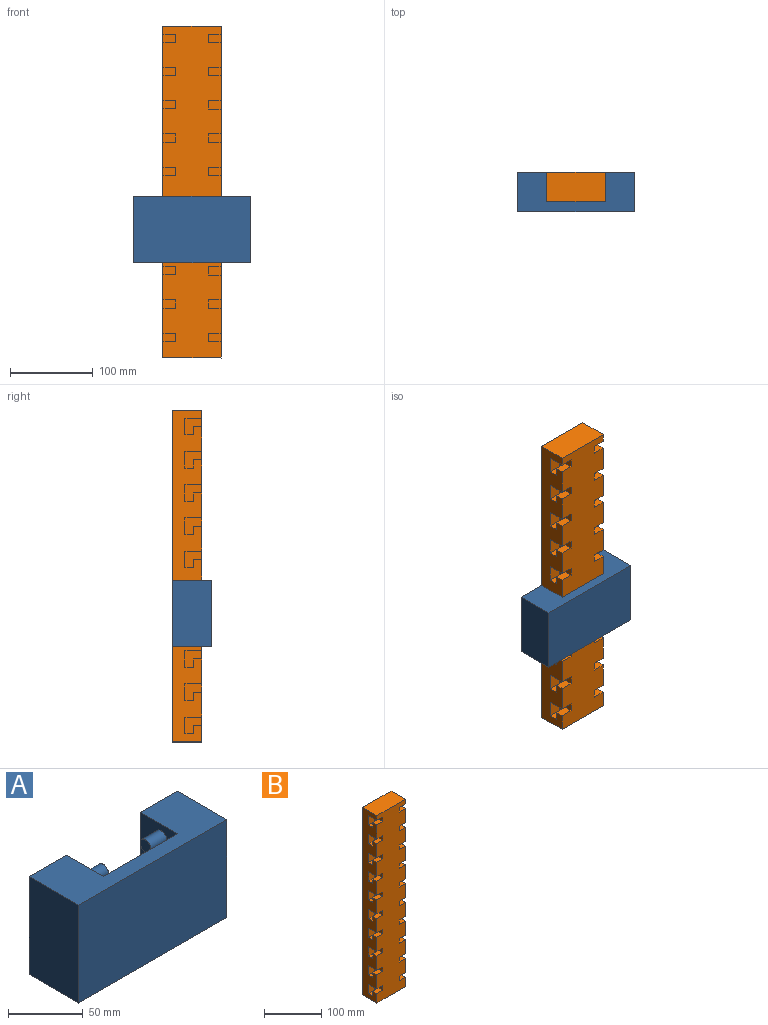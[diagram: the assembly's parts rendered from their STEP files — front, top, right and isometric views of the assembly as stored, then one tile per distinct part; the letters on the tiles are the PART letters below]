
ASSEMBLY  parts=2 mates=1
PART A: 18 faces, bbox 140x47x80 mm
  f0: plane 80x35mm, normal (1,0,0), area 2642.9mm2, adj f1,f3,f9,f10,f12,f16
  f1: plane 140x47mm, normal (0,0,-1), area 4130mm2, adj f0,f2,f3,f4,f5,f6,f9,f11
  f2: plane 80x47mm, normal (-1,0,0), area 3760mm2, adj f1,f3,f10,f11
  f3: plane 80x35mm, normal (0,1,0), area 2800mm2, adj f0,f1,f2,f10
  f4: plane 80x35mm, normal (-1,0,0), area 2642.9mm2, adj f1,f6,f7,f9,f10,f14
  f5: plane 80x47mm, normal (1,0,0), area 3760mm2, adj f1,f6,f10,f11
  f6: plane 80x35mm, normal (0,1,0), area 2800mm2, adj f1,f4,f5,f10
  f7: cylinder r=5mm len=15mm, axis (1,0,0), area 471.2mm2, adj f4,f8
  f8: plane 10x10mm, normal (-1,0,0), area 78.5mm2, adj f7
  f9: plane 80x70mm, normal (0,1,0), area 5600mm2, adj f0,f1,f4,f10
  f10: plane 140x47mm, normal (0,0,1), area 4130mm2, adj f0,f2,f3,f4,f5,f6,f9,f11
  f11: plane 140x80mm, normal (0,-1,0), area 11200mm2, adj f1,f2,f5,f10
  f12: cylinder r=5mm len=15mm, axis (1,0,0), area 471.2mm2, adj f0,f13
  f13: plane 10x10mm, normal (1,0,0), area 78.5mm2, adj f12
  f14: cylinder r=5mm len=15mm, axis (1,0,0), area 471.2mm2, adj f4,f15
  f15: plane 10x10mm, normal (-1,0,0), area 78.5mm2, adj f14
  f16: cylinder r=5mm len=15mm, axis (1,0,0), area 471.2mm2, adj f0,f17
  f17: plane 10x10mm, normal (1,0,0), area 78.5mm2, adj f16
PART B: 126 faces, bbox 70x35x400 mm
  f0: plane 20x15mm, normal (0,-1,0), area 300mm2, adj f1,f2,f7,f16
  f1: plane 20x15mm, normal (0,0,-1), area 300mm2, adj f0,f7,f8,f16
  f2: plane 15x10mm, normal (0,0,1), area 150mm2, adj f0,f7,f13,f16
  f3: plane 15x10mm, normal (0,0,1), area 150mm2, adj f4,f5,f8,f15
  f4: plane 15x10mm, normal (0,1,0), area 150mm2, adj f3,f5,f14,f15
  f5: plane 400x35mm, normal (-1,0,0), area 11000mm2, adj f3,f4,f6,f8,f9,f10,f11,f14
  f6: plane 70x35mm, normal (0,0,-1), area 2450mm2, adj f5,f7,f8,f9
  f7: plane 400x35mm, normal (1,0,0), area 11000mm2, adj f0,f1,f2,f6,f8,f9,f12,f13
  f8: plane 400x70mm, normal (0,-1,0), area 25000mm2, adj f1,f3,f5,f6,f7,f11,f12,f15
  f9: plane 400x70mm, normal (0,1,0), area 28000mm2, adj f5,f6,f7,f118
  f10: plane 20x15mm, normal (0,-1,0), area 300mm2, adj f5,f11,f14,f15
  f11: plane 20x15mm, normal (0,0,-1), area 300mm2, adj f5,f8,f10,f15
  f12: plane 15x10mm, normal (0,0,1), area 150mm2, adj f7,f8,f13,f16
  f13: plane 15x10mm, normal (0,1,0), area 150mm2, adj f2,f7,f12,f16
  f14: plane 15x10mm, normal (0,0,1), area 150mm2, adj f4,f5,f10,f15
  f15: plane 20x20mm, normal (-1,0,0), area 300mm2, adj f3,f4,f8,f10,f11,f14
  f16: plane 20x20mm, normal (1,0,0), area 300mm2, adj f0,f1,f2,f8,f12,f13
  f17: plane 20x15mm, normal (0,-1,0), area 300mm2, adj f7,f18,f19,f28
  f18: plane 20x15mm, normal (0,0,-1), area 300mm2, adj f7,f8,f17,f28
  f19: plane 15x10mm, normal (0,0,1), area 150mm2, adj f7,f17,f25,f28
  f20: plane 15x10mm, normal (0,0,1), area 150mm2, adj f5,f8,f21,f27
  f21: plane 15x10mm, normal (0,1,0), area 150mm2, adj f5,f20,f26,f27
  f22: plane 20x15mm, normal (0,-1,0), area 300mm2, adj f5,f23,f26,f27
  f23: plane 20x15mm, normal (0,0,-1), area 300mm2, adj f5,f8,f22,f27
  f24: plane 15x10mm, normal (0,0,1), area 150mm2, adj f7,f8,f25,f28
  f25: plane 15x10mm, normal (0,1,0), area 150mm2, adj f7,f19,f24,f28
  f26: plane 15x10mm, normal (0,0,1), area 150mm2, adj f5,f21,f22,f27
  f27: plane 20x20mm, normal (-1,0,0), area 300mm2, adj f8,f20,f21,f22,f23,f26
  f28: plane 20x20mm, normal (1,0,0), area 300mm2, adj f8,f17,f18,f19,f24,f25
  f29: plane 20x15mm, normal (0,-1,0), area 300mm2, adj f7,f30,f31,f40
  f30: plane 20x15mm, normal (0,0,-1), area 300mm2, adj f7,f8,f29,f40
  f31: plane 15x10mm, normal (0,0,1), area 150mm2, adj f7,f29,f37,f40
  f32: plane 15x10mm, normal (0,0,1), area 150mm2, adj f5,f8,f33,f39
  f33: plane 15x10mm, normal (0,1,0), area 150mm2, adj f5,f32,f38,f39
  f34: plane 20x15mm, normal (0,-1,0), area 300mm2, adj f5,f35,f38,f39
  f35: plane 20x15mm, normal (0,0,-1), area 300mm2, adj f5,f8,f34,f39
  f36: plane 15x10mm, normal (0,0,1), area 150mm2, adj f7,f8,f37,f40
  f37: plane 15x10mm, normal (0,1,0), area 150mm2, adj f7,f31,f36,f40
  f38: plane 15x10mm, normal (0,0,1), area 150mm2, adj f5,f33,f34,f39
  f39: plane 20x20mm, normal (-1,0,0), area 300mm2, adj f8,f32,f33,f34,f35,f38
  f40: plane 20x20mm, normal (1,0,0), area 300mm2, adj f8,f29,f30,f31,f36,f37
  f41: plane 20x15mm, normal (0,-1,0), area 300mm2, adj f7,f42,f43,f52
  f42: plane 20x15mm, normal (0,0,-1), area 300mm2, adj f7,f8,f41,f52
  f43: plane 15x10mm, normal (0,0,1), area 150mm2, adj f7,f41,f49,f52
  f44: plane 15x10mm, normal (0,0,1), area 150mm2, adj f5,f8,f45,f51
  f45: plane 15x10mm, normal (0,1,0), area 150mm2, adj f5,f44,f50,f51
  f46: plane 20x15mm, normal (0,-1,0), area 300mm2, adj f5,f47,f50,f51
  f47: plane 20x15mm, normal (0,0,-1), area 300mm2, adj f5,f8,f46,f51
  f48: plane 15x10mm, normal (0,0,1), area 150mm2, adj f7,f8,f49,f52
  f49: plane 15x10mm, normal (0,1,0), area 150mm2, adj f7,f43,f48,f52
  f50: plane 15x10mm, normal (0,0,1), area 150mm2, adj f5,f45,f46,f51
  f51: plane 20x20mm, normal (-1,0,0), area 300mm2, adj f8,f44,f45,f46,f47,f50
  f52: plane 20x20mm, normal (1,0,0), area 300mm2, adj f8,f41,f42,f43,f48,f49
  f53: plane 20x15mm, normal (0,-1,0), area 300mm2, adj f7,f54,f55,f64
  f54: plane 20x15mm, normal (0,0,-1), area 300mm2, adj f7,f8,f53,f64
  f55: plane 15x10mm, normal (0,0,1), area 150mm2, adj f7,f53,f61,f64
  f56: plane 15x10mm, normal (0,0,1), area 150mm2, adj f5,f8,f57,f63
  f57: plane 15x10mm, normal (0,1,0), area 150mm2, adj f5,f56,f62,f63
  f58: plane 20x15mm, normal (0,-1,0), area 300mm2, adj f5,f59,f62,f63
  f59: plane 20x15mm, normal (0,0,-1), area 300mm2, adj f5,f8,f58,f63
  f60: plane 15x10mm, normal (0,0,1), area 150mm2, adj f7,f8,f61,f64
  f61: plane 15x10mm, normal (0,1,0), area 150mm2, adj f7,f55,f60,f64
  f62: plane 15x10mm, normal (0,0,1), area 150mm2, adj f5,f57,f58,f63
  f63: plane 20x20mm, normal (-1,0,0), area 300mm2, adj f8,f56,f57,f58,f59,f62
  f64: plane 20x20mm, normal (1,0,0), area 300mm2, adj f8,f53,f54,f55,f60,f61
  f65: plane 20x15mm, normal (0,-1,0), area 300mm2, adj f7,f66,f67,f76
  f66: plane 20x15mm, normal (0,0,-1), area 300mm2, adj f7,f8,f65,f76
  f67: plane 15x10mm, normal (0,0,1), area 150mm2, adj f7,f65,f73,f76
  f68: plane 15x10mm, normal (0,0,1), area 150mm2, adj f5,f8,f69,f75
  f69: plane 15x10mm, normal (0,1,0), area 150mm2, adj f5,f68,f74,f75
  f70: plane 20x15mm, normal (0,-1,0), area 300mm2, adj f5,f71,f74,f75
  f71: plane 20x15mm, normal (0,0,-1), area 300mm2, adj f5,f8,f70,f75
  f72: plane 15x10mm, normal (0,0,1), area 150mm2, adj f7,f8,f73,f76
  f73: plane 15x10mm, normal (0,1,0), area 150mm2, adj f7,f67,f72,f76
  f74: plane 15x10mm, normal (0,0,1), area 150mm2, adj f5,f69,f70,f75
  f75: plane 20x20mm, normal (-1,0,0), area 300mm2, adj f8,f68,f69,f70,f71,f74
  f76: plane 20x20mm, normal (1,0,0), area 300mm2, adj f8,f65,f66,f67,f72,f73
  f77: plane 20x15mm, normal (0,-1,0), area 300mm2, adj f7,f78,f79,f88
  f78: plane 20x15mm, normal (0,0,-1), area 300mm2, adj f7,f8,f77,f88
  f79: plane 15x10mm, normal (0,0,1), area 150mm2, adj f7,f77,f85,f88
  f80: plane 15x10mm, normal (0,0,1), area 150mm2, adj f5,f8,f81,f87
  f81: plane 15x10mm, normal (0,1,0), area 150mm2, adj f5,f80,f86,f87
  f82: plane 20x15mm, normal (0,-1,0), area 300mm2, adj f5,f83,f86,f87
  f83: plane 20x15mm, normal (0,0,-1), area 300mm2, adj f5,f8,f82,f87
  f84: plane 15x10mm, normal (0,0,1), area 150mm2, adj f7,f8,f85,f88
  f85: plane 15x10mm, normal (0,1,0), area 150mm2, adj f7,f79,f84,f88
  f86: plane 15x10mm, normal (0,0,1), area 150mm2, adj f5,f81,f82,f87
  f87: plane 20x20mm, normal (-1,0,0), area 300mm2, adj f8,f80,f81,f82,f83,f86
  f88: plane 20x20mm, normal (1,0,0), area 300mm2, adj f8,f77,f78,f79,f84,f85
  f89: plane 20x15mm, normal (0,-1,0), area 300mm2, adj f7,f90,f91,f100
  f90: plane 20x15mm, normal (0,0,-1), area 300mm2, adj f7,f8,f89,f100
  f91: plane 15x10mm, normal (0,0,1), area 150mm2, adj f7,f89,f97,f100
  f92: plane 15x10mm, normal (0,0,1), area 150mm2, adj f5,f8,f93,f99
  f93: plane 15x10mm, normal (0,1,0), area 150mm2, adj f5,f92,f98,f99
  f94: plane 20x15mm, normal (0,-1,0), area 300mm2, adj f5,f95,f98,f99
  f95: plane 20x15mm, normal (0,0,-1), area 300mm2, adj f5,f8,f94,f99
  f96: plane 15x10mm, normal (0,0,1), area 150mm2, adj f7,f8,f97,f100
  f97: plane 15x10mm, normal (0,1,0), area 150mm2, adj f7,f91,f96,f100
  f98: plane 15x10mm, normal (0,0,1), area 150mm2, adj f5,f93,f94,f99
  f99: plane 20x20mm, normal (-1,0,0), area 300mm2, adj f8,f92,f93,f94,f95,f98
  f100: plane 20x20mm, normal (1,0,0), area 300mm2, adj f8,f89,f90,f91,f96,f97
  f101: plane 20x15mm, normal (0,-1,0), area 300mm2, adj f7,f102,f103,f112
  f102: plane 20x15mm, normal (0,0,-1), area 300mm2, adj f7,f8,f101,f112
  f103: plane 15x10mm, normal (0,0,1), area 150mm2, adj f7,f101,f109,f112
  f104: plane 15x10mm, normal (0,0,1), area 150mm2, adj f5,f8,f105,f111
  f105: plane 15x10mm, normal (0,1,0), area 150mm2, adj f5,f104,f110,f111
  f106: plane 20x15mm, normal (0,-1,0), area 300mm2, adj f5,f107,f110,f111
  f107: plane 20x15mm, normal (0,0,-1), area 300mm2, adj f5,f8,f106,f111
  f108: plane 15x10mm, normal (0,0,1), area 150mm2, adj f7,f8,f109,f112
  f109: plane 15x10mm, normal (0,1,0), area 150mm2, adj f7,f103,f108,f112
  f110: plane 15x10mm, normal (0,0,1), area 150mm2, adj f5,f105,f106,f111
  f111: plane 20x20mm, normal (-1,0,0), area 300mm2, adj f8,f104,f105,f106,f107,f110
  f112: plane 20x20mm, normal (1,0,0), area 300mm2, adj f8,f101,f102,f103,f108,f109
  f113: plane 20x15mm, normal (0,-1,0), area 300mm2, adj f7,f114,f115,f125
  f114: plane 20x15mm, normal (0,0,-1), area 300mm2, adj f7,f8,f113,f125
  f115: plane 15x10mm, normal (0,0,1), area 150mm2, adj f7,f113,f122,f125
  f116: plane 15x10mm, normal (0,0,1), area 150mm2, adj f5,f8,f117,f124
  f117: plane 15x10mm, normal (0,1,0), area 150mm2, adj f5,f116,f123,f124
  f118: plane 70x35mm, normal (0,0,1), area 2450mm2, adj f5,f7,f8,f9
  f119: plane 20x15mm, normal (0,-1,0), area 300mm2, adj f5,f120,f123,f124
  f120: plane 20x15mm, normal (0,0,-1), area 300mm2, adj f5,f8,f119,f124
  f121: plane 15x10mm, normal (0,0,1), area 150mm2, adj f7,f8,f122,f125
  f122: plane 15x10mm, normal (0,1,0), area 150mm2, adj f7,f115,f121,f125
  f123: plane 15x10mm, normal (0,0,1), area 150mm2, adj f5,f117,f119,f124
  f124: plane 20x20mm, normal (-1,0,0), area 300mm2, adj f8,f116,f117,f119,f120,f123
  f125: plane 20x20mm, normal (1,0,0), area 300mm2, adj f8,f113,f114,f115,f121,f122
PLACE A t=(235.13,7.72,38.7)mm
PLACE B t=(38.8,42.72,45.64)mm fixed
MATE pin_slot A.f12 <-> B.f63  axis (1,0,0) through (53.8,22.72,190.64)mm
